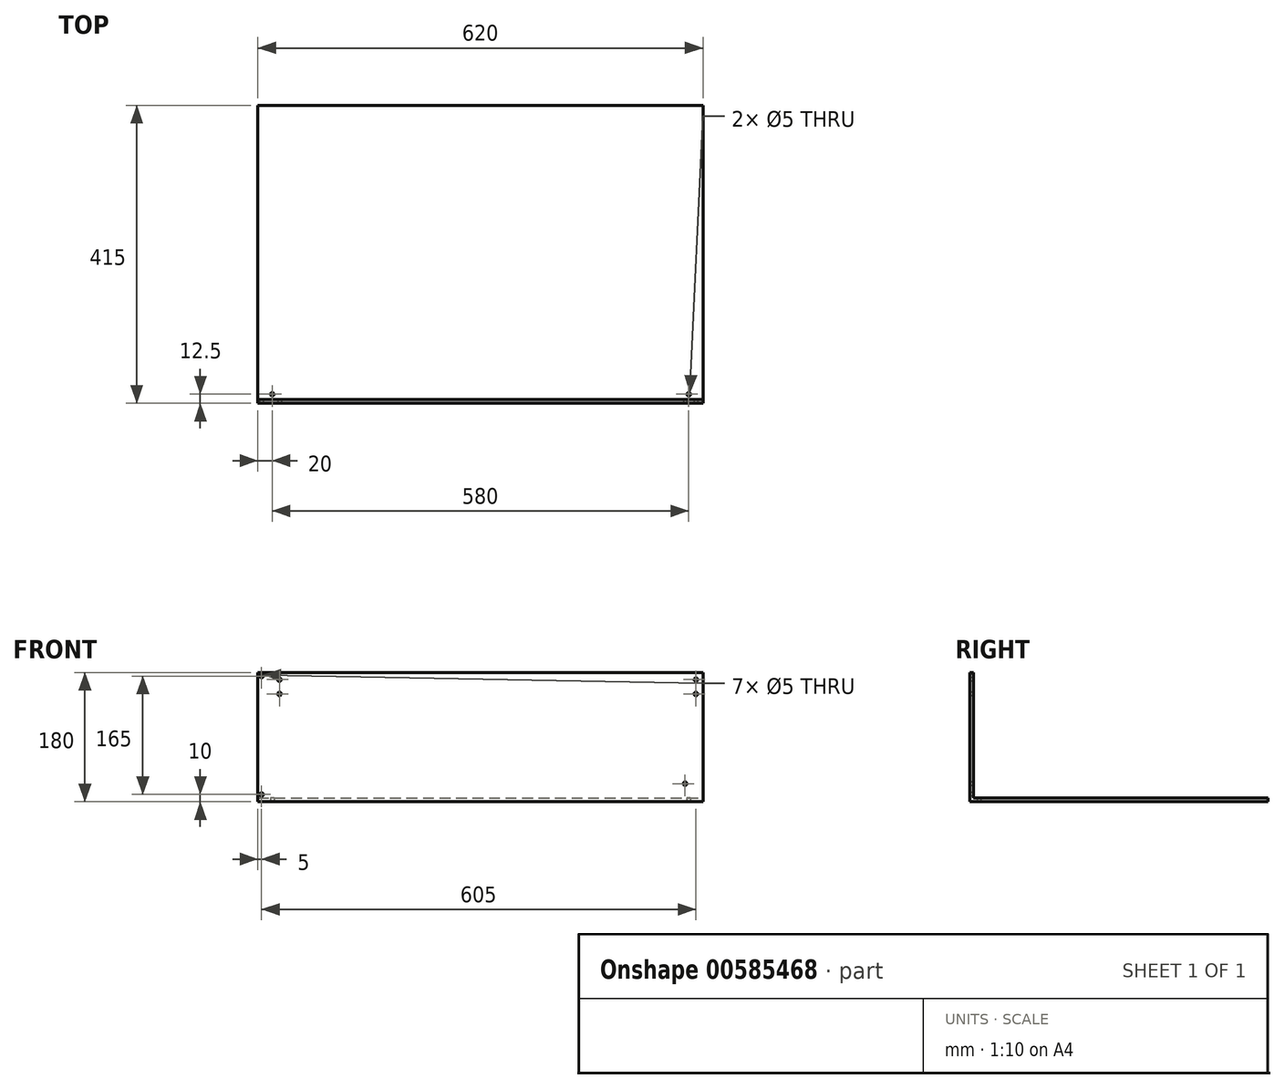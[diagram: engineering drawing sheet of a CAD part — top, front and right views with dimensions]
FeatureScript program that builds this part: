
annotation { "Feature Type Name" : "Feature", "Feature Type Description" : "" }
export const myFeature = defineFeature(function(context is Context, id is Id, definition is map)
    precondition{}
    {
        {
            var Q0;
            Q0=qCreatedBy(makeId("Top.planeOp"),FACE);
            var sketch = newSketch(context, id + "F0", { "sketchPlane" : qUnion([Q0])});
            skLineSegment(sketch, "E0.bottom", {"start": v(310, -207.5) * mm, "end": v(-310, -207.5) * mm});
            skLineSegment(sketch, "E0.top", {"start": v(310, 207.5) * mm, "end": v(-310, 207.5) * mm});
            skLineSegment(sketch, "E0.left", {"start": v(310, -207.5) * mm, "end": v(310, 207.5) * mm});
            skLineSegment(sketch, "E0.right", {"start": v(-310, -207.5) * mm, "end": v(-310, 207.5) * mm});
            skPoint(sketch, "E0.middle", {"position": v(0, 0) * mm});
            skSolve(sketch);
        }
        {
            var Q0;
            Q0 = qSketchRegion(id + "F0", true);
            extrude(context, id + "F1", {"entities" : qUnion([Q0]), "depth" : 5 * mm, "offsetDistance" : 25 * mm});
        }
        {
            var Q0;
            Q0=makeQuery(id+"F1.opExtrude","CAP_FACE",FACE,{"disambiguationData":[OSD([sQuery(id+"F0.wireOp",EDGE,"E0.bottom"),sQuery(id+"F0.wireOp",EDGE,"E0.top"),sQuery(id+"F0.wireOp",EDGE,"E0.left"),sQuery(id+"F0.wireOp",EDGE,"E0.right")])],"isStart":false});
            var sketch = newSketch(context, id + "F2", { "sketchPlane" : qUnion([Q0])});
            skLineSegment(sketch, "E1", {"start": v(-310, -202.5) * mm, "end": v(310, -202.5) * mm});
            skLineSegment(sketch, "E2", {"start": v(310, -202.5) * mm, "end": v(310, -207.5) * mm});
            skLineSegment(sketch, "E3", {"start": v(310, -207.5) * mm, "end": v(-310, -207.5) * mm});
            skLineSegment(sketch, "E4", {"start": v(-310, -207.5) * mm, "end": v(-310, -202.5) * mm});
            skSolve(sketch);
        }
        {
            var Q0;
            Q0=makeQuery(id+"F2.imprint","IMPRINT",FACE,{"disambiguationData":[TD([[makeQuery(id+"F2.imprint","IMPRINT",EDGE,{"derivedFrom":sQuery(id+"F2.wireOp",EDGE,"E1")}),-1.0]])]});
            extrude(context, id + "F3", {"entities" : qUnion([Q0]), "operationType" : NewBodyOperationType.ADD, "depth" : 175 * mm, "offsetDistance" : 25 * mm});
        }
        {
            var Q0;
            Q0=makeQuery(id+"F3.boolean.opBoolean","MERGE",FACE,{"derivedFrom":[makeQuery(id+"F1.opExtrude","SWEPT_FACE",FACE,{"disambiguationData":[OSD([sQuery(id+"F0.wireOp",EDGE,"E0.bottom")])]}),makeQuery(id+"F3.opExtrude","SWEPT_FACE",FACE,{"disambiguationData":[OSD([sQuery(id+"F2.wireOp",EDGE,"E3")])]})]});
            var sketch = newSketch(context, id + "F4", { "sketchPlane" : qUnion([Q0])});
            skLineSegment(sketch, "E5", {"start": v(300, 180) * mm, "end": v(300, 138.82) * mm, "construction": true});
            skPoint(sketch, "E6", {"position": v(300, 170) * mm});
            skPoint(sketch, "E7", {"position": v(300, 150) * mm});
            skSolve(sketch);
        }
        {
            var Q0;
            Q0=sQuery(id+"F4.wireOp",VERTEX,"E6");
            var Q1;
            Q1=makeQuery(id+"F1.opExtrude","SWEPT_BODY",BODY,{"disambiguationData":[OSD([sQuery(id+"F0.wireOp",EDGE,"E0.bottom"),sQuery(id+"F0.wireOp",EDGE,"E0.top"),sQuery(id+"F0.wireOp",EDGE,"E0.left"),sQuery(id+"F0.wireOp",EDGE,"E0.right")])]});
            hole(context, id + "F5", {"style" : HoleStyle.SIMPLE, "endStyle" : HoleEndStyle.THROUGH, "holeDiameter" : 5 * mm, "majorDiameter" : 5 * mm, "isTappedThrough" : true, "tappedDepth" : 12 * mm, "tapClearance" : 3, "locations" : qUnion([Q0]), "scope" : qUnion([Q1])});
        }
        {
            var Q0;
            Q0=makeQuery(id+"F3.boolean.opBoolean","MERGE",FACE,{"derivedFrom":[makeQuery(id+"F1.opExtrude","SWEPT_FACE",FACE,{"disambiguationData":[OSD([sQuery(id+"F0.wireOp",EDGE,"E0.bottom")])]}),makeQuery(id+"F3.opExtrude","SWEPT_FACE",FACE,{"disambiguationData":[OSD([sQuery(id+"F2.wireOp",EDGE,"E3")])]})]});
            var sketch = newSketch(context, id + "F6", { "sketchPlane" : qUnion([Q0])});
            skLineSegment(sketch, "E8", {"start": v(300, 180) * mm, "end": v(300, 144.67) * mm, "construction": true});
            skPoint(sketch, "E9", {"position": v(300, 150) * mm});
            skSolve(sketch);
        }
        {
            var Q0;
            Q0=sQuery(id+"F6.wireOp",VERTEX,"E9");
            var Q1;
            Q1=makeQuery(id+"F1.opExtrude","SWEPT_BODY",BODY,{"disambiguationData":[OSD([sQuery(id+"F0.wireOp",EDGE,"E0.bottom"),sQuery(id+"F0.wireOp",EDGE,"E0.top"),sQuery(id+"F0.wireOp",EDGE,"E0.left"),sQuery(id+"F0.wireOp",EDGE,"E0.right")])]});
            hole(context, id + "F7", {"style" : HoleStyle.SIMPLE, "endStyle" : HoleEndStyle.THROUGH, "holeDiameter" : 5 * mm, "majorDiameter" : 5 * mm, "isTappedThrough" : true, "tappedDepth" : 12 * mm, "tapClearance" : 3, "locations" : qUnion([Q0]), "scope" : qUnion([Q1])});
        }
        {
            var Q0;
            Q0=makeQuery(id+"F3.boolean.opBoolean","MERGE",FACE,{"derivedFrom":[makeQuery(id+"F1.opExtrude","SWEPT_FACE",FACE,{"disambiguationData":[OSD([sQuery(id+"F0.wireOp",EDGE,"E0.bottom")])]}),makeQuery(id+"F3.opExtrude","SWEPT_FACE",FACE,{"disambiguationData":[OSD([sQuery(id+"F2.wireOp",EDGE,"E3")])]})]});
            var sketch = newSketch(context, id + "F8", { "sketchPlane" : qUnion([Q0])});
            skLineSegment(sketch, "E10", {"start": v(-280, 180) * mm, "end": v(-280, 162.68) * mm, "construction": true});
            skPoint(sketch, "E11", {"position": v(-280, 170) * mm});
            skSolve(sketch);
        }
        {
            var Q0;
            Q0=sQuery(id+"F8.wireOp",VERTEX,"E11");
            var Q1;
            Q1=makeQuery(id+"F1.opExtrude","SWEPT_BODY",BODY,{"disambiguationData":[OSD([sQuery(id+"F0.wireOp",EDGE,"E0.bottom"),sQuery(id+"F0.wireOp",EDGE,"E0.top"),sQuery(id+"F0.wireOp",EDGE,"E0.left"),sQuery(id+"F0.wireOp",EDGE,"E0.right")])]});
            hole(context, id + "F9", {"style" : HoleStyle.SIMPLE, "endStyle" : HoleEndStyle.THROUGH, "holeDiameter" : 5 * mm, "majorDiameter" : 5 * mm, "isTappedThrough" : true, "tappedDepth" : 12 * mm, "tapClearance" : 3, "locations" : qUnion([Q0]), "scope" : qUnion([Q1])});
        }
        {
            var Q0;
            Q0=makeQuery(id+"F3.boolean.opBoolean","MERGE",FACE,{"derivedFrom":[makeQuery(id+"F1.opExtrude","SWEPT_FACE",FACE,{"disambiguationData":[OSD([sQuery(id+"F0.wireOp",EDGE,"E0.bottom")])]}),makeQuery(id+"F3.opExtrude","SWEPT_FACE",FACE,{"disambiguationData":[OSD([sQuery(id+"F2.wireOp",EDGE,"E3")])]})]});
            var sketch = newSketch(context, id + "F10", { "sketchPlane" : qUnion([Q0])});
            skLineSegment(sketch, "E12", {"start": v(-280, 180) * mm, "end": v(-280, 135.53) * mm, "construction": true});
            skPoint(sketch, "E13", {"position": v(-280, 150) * mm});
            skSolve(sketch);
        }
        {
            var Q0;
            Q0=sQuery(id+"F10.wireOp",VERTEX,"E13");
            var Q1;
            Q1=makeQuery(id+"F1.opExtrude","SWEPT_BODY",BODY,{"disambiguationData":[OSD([sQuery(id+"F0.wireOp",EDGE,"E0.bottom"),sQuery(id+"F0.wireOp",EDGE,"E0.top"),sQuery(id+"F0.wireOp",EDGE,"E0.left"),sQuery(id+"F0.wireOp",EDGE,"E0.right")])]});
            hole(context, id + "F11", {"style" : HoleStyle.SIMPLE, "endStyle" : HoleEndStyle.THROUGH, "holeDiameter" : 5 * mm, "majorDiameter" : 5 * mm, "isTappedThrough" : true, "tappedDepth" : 12 * mm, "tapClearance" : 3, "locations" : qUnion([Q0]), "scope" : qUnion([Q1])});
        }
        {
            var Q0;
            Q0=makeQuery(id+"F3.boolean.opBoolean","MERGE",FACE,{"derivedFrom":[makeQuery(id+"F1.opExtrude","SWEPT_FACE",FACE,{"disambiguationData":[OSD([sQuery(id+"F0.wireOp",EDGE,"E0.bottom")])]}),makeQuery(id+"F3.opExtrude","SWEPT_FACE",FACE,{"disambiguationData":[OSD([sQuery(id+"F2.wireOp",EDGE,"E3")])]})]});
            var sketch = newSketch(context, id + "F12", { "sketchPlane" : qUnion([Q0])});
            skLineSegment(sketch, "E14", {"start": v(-310, 175) * mm, "end": v(-305, 175) * mm});
            skSolve(sketch);
        }
        {
            var Q0;
            Q0=sQuery(id+"F12.wireOp",VERTEX,"E14.end");
            var Q1;
            Q1=makeQuery(id+"F1.opExtrude","SWEPT_BODY",BODY,{"disambiguationData":[OSD([sQuery(id+"F0.wireOp",EDGE,"E0.bottom"),sQuery(id+"F0.wireOp",EDGE,"E0.top"),sQuery(id+"F0.wireOp",EDGE,"E0.left"),sQuery(id+"F0.wireOp",EDGE,"E0.right")])]});
            hole(context, id + "F13", {"style" : HoleStyle.SIMPLE, "endStyle" : HoleEndStyle.THROUGH, "holeDiameter" : 5 * mm, "majorDiameter" : 5 * mm, "isTappedThrough" : true, "tappedDepth" : 12 * mm, "tapClearance" : 3, "locations" : qUnion([Q0]), "scope" : qUnion([Q1])});
        }
        {
            var Q0;
            Q0=makeQuery(id+"F3.boolean.opBoolean","MERGE",FACE,{"derivedFrom":[makeQuery(id+"F1.opExtrude","SWEPT_FACE",FACE,{"disambiguationData":[OSD([sQuery(id+"F0.wireOp",EDGE,"E0.bottom")])]}),makeQuery(id+"F3.opExtrude","SWEPT_FACE",FACE,{"disambiguationData":[OSD([sQuery(id+"F2.wireOp",EDGE,"E3")])]})]});
            var sketch = newSketch(context, id + "F14", { "sketchPlane" : qUnion([Q0])});
            skLineSegment(sketch, "E15", {"start": v(-310, 10) * mm, "end": v(-305, 10) * mm});
            skSolve(sketch);
        }
        {
            var Q0;
            Q0=sQuery(id+"F14.wireOp",VERTEX,"E15.end");
            var Q1;
            Q1=makeQuery(id+"F1.opExtrude","SWEPT_BODY",BODY,{"disambiguationData":[OSD([sQuery(id+"F0.wireOp",EDGE,"E0.bottom"),sQuery(id+"F0.wireOp",EDGE,"E0.top"),sQuery(id+"F0.wireOp",EDGE,"E0.left"),sQuery(id+"F0.wireOp",EDGE,"E0.right")])]});
            hole(context, id + "F15", {"style" : HoleStyle.SIMPLE, "endStyle" : HoleEndStyle.THROUGH, "holeDiameter" : 5 * mm, "majorDiameter" : 5 * mm, "isTappedThrough" : true, "tappedDepth" : 12 * mm, "tapClearance" : 3, "locations" : qUnion([Q0]), "scope" : qUnion([Q1])});
        }
        {
            var Q0;
            Q0=makeQuery(id+"F1.opExtrude","CAP_FACE",FACE,{"disambiguationData":[OSD([sQuery(id+"F0.wireOp",EDGE,"E0.bottom"),sQuery(id+"F0.wireOp",EDGE,"E0.top"),sQuery(id+"F0.wireOp",EDGE,"E0.left"),sQuery(id+"F0.wireOp",EDGE,"E0.right")])],"isStart":true});
            var sketch = newSketch(context, id + "F16", { "sketchPlane" : qUnion([Q0])});
            skLineSegment(sketch, "E16", {"start": v(290, 207.5) * mm, "end": v(290, 195) * mm});
            skSolve(sketch);
        }
        {
            var Q0;
            Q0=sQuery(id+"F16.wireOp",VERTEX,"E16.end");
            var Q1;
            Q1=makeQuery(id+"F1.opExtrude","SWEPT_BODY",BODY,{"disambiguationData":[OSD([sQuery(id+"F0.wireOp",EDGE,"E0.bottom"),sQuery(id+"F0.wireOp",EDGE,"E0.top"),sQuery(id+"F0.wireOp",EDGE,"E0.left"),sQuery(id+"F0.wireOp",EDGE,"E0.right")])]});
            hole(context, id + "F17", {"style" : HoleStyle.SIMPLE, "endStyle" : HoleEndStyle.THROUGH, "holeDiameter" : 5 * mm, "majorDiameter" : 5 * mm, "isTappedThrough" : true, "tappedDepth" : 12 * mm, "tapClearance" : 3, "locations" : qUnion([Q0]), "scope" : qUnion([Q1])});
        }
        {
            var Q0;
            Q0=makeQuery(id+"F1.opExtrude","CAP_FACE",FACE,{"disambiguationData":[OSD([sQuery(id+"F0.wireOp",EDGE,"E0.bottom"),sQuery(id+"F0.wireOp",EDGE,"E0.top"),sQuery(id+"F0.wireOp",EDGE,"E0.left"),sQuery(id+"F0.wireOp",EDGE,"E0.right")])],"isStart":true});
            var sketch = newSketch(context, id + "F18", { "sketchPlane" : qUnion([Q0])});
            skLineSegment(sketch, "E17", {"start": v(-290, 207.5) * mm, "end": v(-290, 195) * mm});
            skSolve(sketch);
        }
        {
            var Q0;
            Q0=sQuery(id+"F18.wireOp",VERTEX,"E17.end");
            var Q1;
            Q1=makeQuery(id+"F1.opExtrude","SWEPT_BODY",BODY,{"disambiguationData":[OSD([sQuery(id+"F0.wireOp",EDGE,"E0.bottom"),sQuery(id+"F0.wireOp",EDGE,"E0.top"),sQuery(id+"F0.wireOp",EDGE,"E0.left"),sQuery(id+"F0.wireOp",EDGE,"E0.right")])]});
            hole(context, id + "F19", {"style" : HoleStyle.SIMPLE, "endStyle" : HoleEndStyle.THROUGH, "holeDiameter" : 5 * mm, "majorDiameter" : 5 * mm, "isTappedThrough" : true, "tappedDepth" : 12 * mm, "tapClearance" : 3, "locations" : qUnion([Q0]), "scope" : qUnion([Q1])});
        }
        {
            var Q0;
            Q0=makeQuery(id+"F3.boolean.opBoolean","MERGE",FACE,{"derivedFrom":[makeQuery(id+"F1.opExtrude","SWEPT_FACE",FACE,{"disambiguationData":[OSD([sQuery(id+"F0.wireOp",EDGE,"E0.bottom")])]}),makeQuery(id+"F3.opExtrude","SWEPT_FACE",FACE,{"disambiguationData":[OSD([sQuery(id+"F2.wireOp",EDGE,"E3")])]})]});
            var sketch = newSketch(context, id + "F20", { "sketchPlane" : qUnion([Q0])});
            skLineSegment(sketch, "E18", {"start": v(285, 0) * mm, "end": v(285, 25) * mm});
            skSolve(sketch);
        }
        {
            var Q0;
            Q0=sQuery(id+"F20.wireOp",VERTEX,"E18.end");
            var Q1;
            Q1=makeQuery(id+"F1.opExtrude","SWEPT_BODY",BODY,{"disambiguationData":[OSD([sQuery(id+"F0.wireOp",EDGE,"E0.bottom"),sQuery(id+"F0.wireOp",EDGE,"E0.top"),sQuery(id+"F0.wireOp",EDGE,"E0.left"),sQuery(id+"F0.wireOp",EDGE,"E0.right")])]});
            hole(context, id + "F21", {"style" : HoleStyle.SIMPLE, "endStyle" : HoleEndStyle.BLIND, "holeDiameter" : 5 * mm, "majorDiameter" : 5 * mm, "holeDepth" : 11 * mm, "isTappedThrough" : true, "tappedDepth" : 12 * mm, "tapClearance" : 3, "locations" : qUnion([Q0]), "scope" : qUnion([Q1])});
        }
    });
